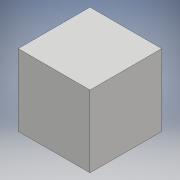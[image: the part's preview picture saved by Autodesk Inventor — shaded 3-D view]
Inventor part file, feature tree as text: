
AUTODESK INVENTOR PART (.ipt)
format: ipt  version: 2017 (Build 210142000, 142)  size: 478,208 bytes
history: native  units: mm
features: extrude x2, sketch x2
ambient origin geometry x8: Origin, YZ Plane, XZ Plane, XY Plane, X Axis, Y Axis, Z Axis, Center Point
bodies: Solid1 (feature_tree)
feature tree (4):
  extrude  "Extrusion1"  Depth=56.65mm TaperAngle=0.0deg
  extrude  "Extrusion2"  [1 undecoded]
  sketch  "Sketch1"  dims[d1=56.65mm d2=56.65mm d3=0.0mm]
  sketch  "Sketch2"  dims[d4=2.0mm d5=0.0mm]
note: 1 required parameter value undecoded (feature->parameter linkage not recoverable at this tier; creation-order binding heuristic only, values carry confidence <= 0.55)
